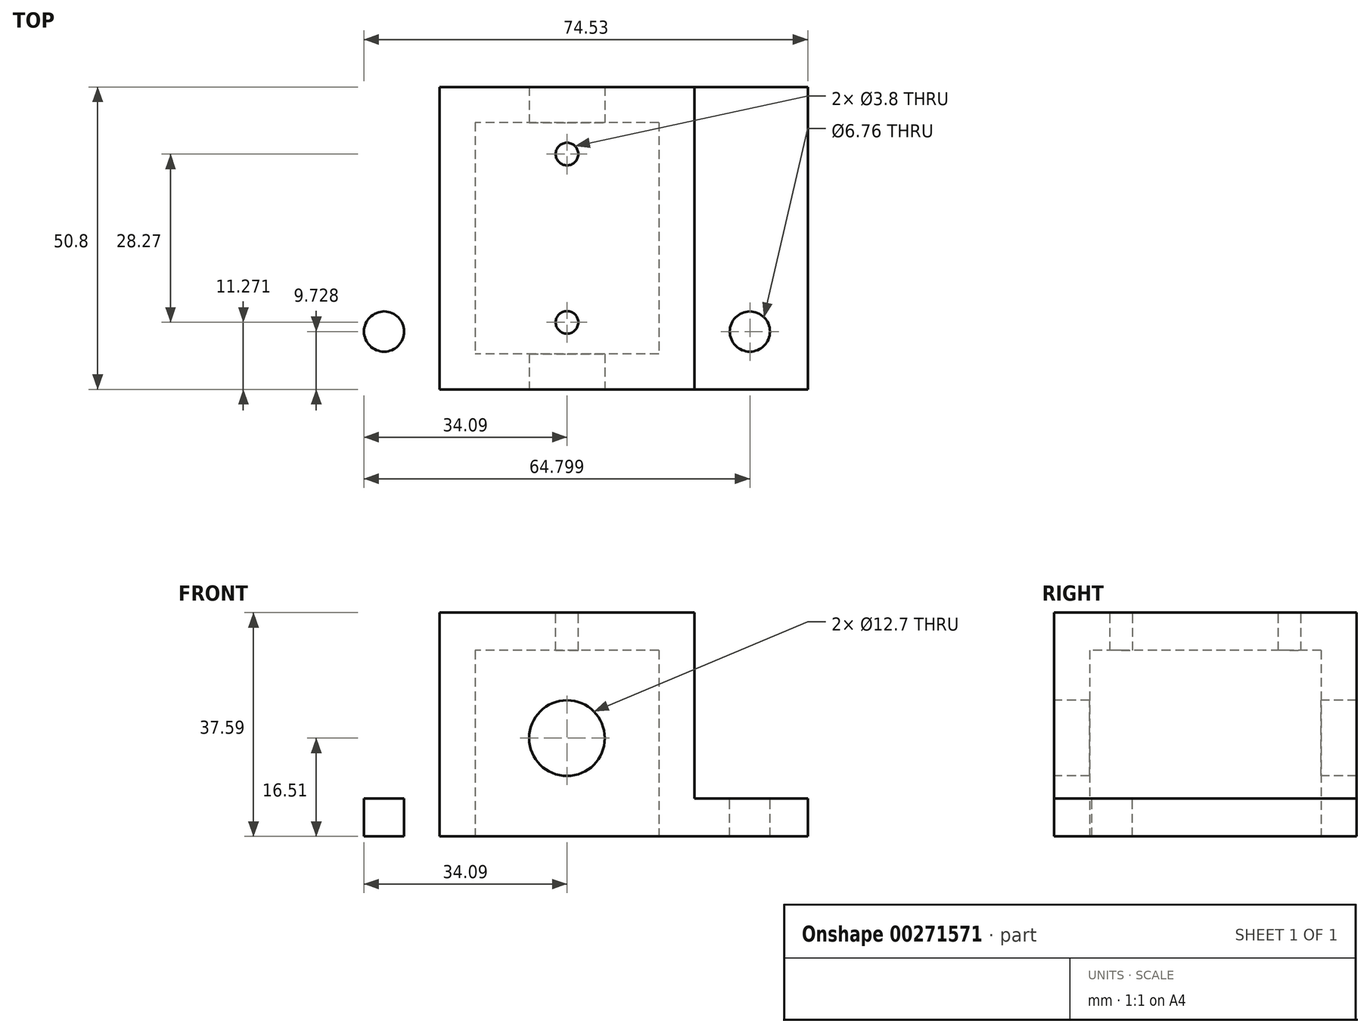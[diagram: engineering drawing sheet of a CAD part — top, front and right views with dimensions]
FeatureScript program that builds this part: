
annotation { "Feature Type Name" : "Feature", "Feature Type Description" : "" }
export const myFeature = defineFeature(function(context is Context, id is Id, definition is map)
    precondition{}
    {
        {
            var Q0;
            Q0=qCreatedBy(makeId("Top.planeOp"),FACE);
            var sketch = newSketch(context, id + "F0", { "sketchPlane" : qUnion([Q0])});
            skLineSegment(sketch, "E0.bottom", {"start": v(40.44, -25.4) * mm, "end": v(-40.44, -25.4) * mm});
            skLineSegment(sketch, "E0.top", {"start": v(40.44, 25.4) * mm, "end": v(-40.44, 25.4) * mm});
            skLineSegment(sketch, "E0.left", {"start": v(40.44, -25.4) * mm, "end": v(40.44, 25.4) * mm});
            skLineSegment(sketch, "E0.right", {"start": v(-40.44, -25.4) * mm, "end": v(-40.44, 25.4) * mm});
            skPoint(sketch, "E0.middle", {"position": v(0, 0) * mm});
            skSolve(sketch);
        }
        {
            var Q0;
            Q0=makeQuery(id+"F0.imprint","IMPRINT",FACE,{"disambiguationData":[TD([[makeQuery(id+"F0.imprint","IMPRINT",EDGE,{"derivedFrom":sQuery(id+"F0.wireOp",EDGE,"E0.bottom")}),-1.0]])]});
            extrude(context, id + "F1", {"entities" : qUnion([Q0]), "depth" : 37.6 * mm});
        }
        {
            var Q0;
            Q0=makeQuery(id+"F1.opExtrude","CAP_FACE",FACE,{"disambiguationData":[OSD([sQuery(id+"F0.wireOp",EDGE,"E0.bottom"),sQuery(id+"F0.wireOp",EDGE,"E0.top"),sQuery(id+"F0.wireOp",EDGE,"E0.left"),sQuery(id+"F0.wireOp",EDGE,"E0.right")])],"isStart":false});
            var sketch = newSketch(context, id + "F2", { "sketchPlane" : qUnion([Q0])});
            skLineSegment(sketch, "E1.left", {"start": v(-40.44, 19.05) * mm, "end": v(-40.44, -19.05) * mm});
            skLineSegment(sketch, "E1.right", {"start": v(-21.39, 19.05) * mm, "end": v(-21.39, -19.05) * mm});
            skLineSegment(sketch, "E2", {"start": v(-21.39, 19.05) * mm, "end": v(-21.39, 25.4) * mm});
            skLineSegment(sketch, "E3", {"start": v(-21.39, -19.05) * mm, "end": v(-21.39, -25.4) * mm});
            skLineSegment(sketch, "E4", {"start": v(0, 15.68) * mm, "end": v(0, -17.66) * mm, "construction": true});
            skLineSegment(sketch, "E5.MirrorCS", {"start": v(21.39, 19.05) * mm, "end": v(21.39, -19.05) * mm});
            skLineSegment(sketch, "E6.MirrorCS", {"start": v(40.44, 19.05) * mm, "end": v(40.44, -19.05) * mm});
            skLineSegment(sketch, "E7", {"start": v(21.39, 19.05) * mm, "end": v(21.39, 25.4) * mm});
            skLineSegment(sketch, "E8", {"start": v(21.39, -19.05) * mm, "end": v(21.39, -25.4) * mm});
            skSolve(sketch);
        }
        {
            var Q0;
            Q0=makeQuery(id+"F2.imprint","IMPRINT",FACE,{"disambiguationData":[TD([[makeQuery(id+"F2.imprint","IMPRINT",EDGE,{"derivedFrom":sQuery(id+"F2.wireOp",EDGE,"E1.bottom")}),-1.0]])]});
            var Q1;
            Q1=makeQuery(id+"F2.imprint","IMPRINT",FACE,{"disambiguationData":[TD([[makeQuery(id+"F2.imprint","IMPRINT",EDGE,{"derivedFrom":sQuery(id+"F2.wireOp",EDGE,"E5.MirrorCS")}),1.0]])]});
            extrude(context, id + "F3", {"entities" : qUnion([Q0, Q1]), "operationType" : NewBodyOperationType.REMOVE, "oppositeDirection" : true, "depth" : 31.24 * mm});
        }
        {
            var Q0;
            Q0=makeQuery(id+"F1.opExtrude","CAP_FACE",FACE,{"disambiguationData":[OSD([sQuery(id+"F0.wireOp",EDGE,"E0.bottom"),sQuery(id+"F0.wireOp",EDGE,"E0.top"),sQuery(id+"F0.wireOp",EDGE,"E0.left"),sQuery(id+"F0.wireOp",EDGE,"E0.right")])],"isStart":true});
            var sketch = newSketch(context, id + "F4", { "sketchPlane" : qUnion([Q0])});
            skLineSegment(sketch, "E9.bottom", {"start": v(15.43, -19.45) * mm, "end": v(-15.43, -19.45) * mm});
            skLineSegment(sketch, "E9.top", {"start": v(15.43, 19.45) * mm, "end": v(-15.43, 19.45) * mm});
            skLineSegment(sketch, "E9.left", {"start": v(15.43, -19.45) * mm, "end": v(15.43, 19.45) * mm});
            skLineSegment(sketch, "E9.right", {"start": v(-15.43, -19.45) * mm, "end": v(-15.43, 19.45) * mm});
            skPoint(sketch, "E9.middle", {"position": v(0, 0) * mm});
            skSolve(sketch);
        }
        {
            var Q0;
            Q0=makeQuery(id+"F4.imprint","IMPRINT",FACE,{"disambiguationData":[TD([[makeQuery(id+"F4.imprint","IMPRINT",EDGE,{"derivedFrom":sQuery(id+"F4.wireOp",EDGE,"E9.bottom")}),-1.0]])]});
            extrude(context, id + "F5", {"entities" : qUnion([Q0]), "operationType" : NewBodyOperationType.REMOVE, "oppositeDirection" : true, "depth" : 31.24 * mm});
        }
        {
            var Q0;
            Q0=makeQuery(id+"F1.opExtrude","SWEPT_FACE",FACE,{"disambiguationData":[OSD([sQuery(id+"F0.wireOp",EDGE,"E0.bottom")])]});
            var sketch = newSketch(context, id + "F6", { "sketchPlane" : qUnion([Q0])});
            skLineSegment(sketch, "E10", {"start": v(-21.38, 6.35) * mm, "end": v(-21.38, 0) * mm, "construction": true});
            skLineSegment(sketch, "E11", {"start": v(21.38, 6.35) * mm, "end": v(21.38, 0) * mm, "construction": true});
            skLineSegment(sketch, "E12", {"start": v(0, 0) * mm, "end": v(0, 10.16) * mm, "construction": true});
            skCircle(sketch, "E13", {"center": v(0, 16.51) * mm, "radius": 6.35 * mm});
            skPoint(sketch, "E13.second.point", {"position": v(0, 22.86) * mm});
            skPoint(sketch, "E13.third.point", {"position": v(6.01, 14.47) * mm});
            skLineSegment(sketch, "E14", {"start": v(0, 16.51) * mm, "end": v(0, 10.16) * mm, "construction": true});
            skSolve(sketch);
        }
        {
            var Q0;
            Q0=makeQuery(id+"F6.imprint","IMPRINT",FACE,{"disambiguationData":[TD([[makeQuery(id+"F6.imprint","IMPRINT",EDGE,{"derivedFrom":sQuery(id+"F6.wireOp",EDGE,"E13")}),1.0]])]});
            extrude(context, id + "F7", {"entities" : qUnion([Q0]), "operationType" : NewBodyOperationType.REMOVE, "oppositeDirection" : true, "depth" : 25400 * mm});
        }
        {
            var Q0;
            {var subQ5=sQuery(id+"F2.wireOp",EDGE,"E1.left");Q0=makeQuery(id+"F2.imprint","IMPRINT",FACE,{"disambiguationData":[TD([[makeQuery(id+"F2.imprint","IMPRINT",EDGE,{"derivedFrom":subQ5}),-1.0]])]});}
            extrude(context, id + "F8", {"entities" : qUnion([Q0]), "operationType" : NewBodyOperationType.REMOVE, "oppositeDirection" : true, "depth" : 31.24 * mm});
        }
        {
            var Q0;
            Q0=makeQuery(id+"F2.imprint","IMPRINT",FACE,{"disambiguationData":[TD([[makeQuery(id+"F2.imprint","IMPRINT",EDGE,{"derivedFrom":sQuery(id+"F2.wireOp",EDGE,"E1.right")}),1.0]])]});
            var sketch = newSketch(context, id + "F9", { "sketchPlane" : qUnion([Q0])});
            skCircle(sketch, "E15", {"center": v(0, 14.14) * mm, "radius": 1.9 * mm});
            skCircle(sketch, "E16", {"center": v(0, -14.13) * mm, "radius": 1.9 * mm});
            skLineSegment(sketch, "E17", {"start": v(0, 12.24) * mm, "end": v(0, -12.23) * mm, "construction": true});
            skSolve(sketch);
        }
        {
            var Q0;
            Q0=makeQuery(id+"F9.imprint","IMPRINT",FACE,{"disambiguationData":[TD([[makeQuery(id+"F9.imprint","IMPRINT",EDGE,{"derivedFrom":sQuery(id+"F9.wireOp",EDGE,"E15")}),1.0]])]});
            var Q1;
            Q1=makeQuery(id+"F9.imprint","IMPRINT",FACE,{"disambiguationData":[TD([[makeQuery(id+"F9.imprint","IMPRINT",EDGE,{"derivedFrom":sQuery(id+"F9.wireOp",EDGE,"E16")}),1.0]])]});
            extrude(context, id + "F10", {"entities" : qUnion([Q0, Q1]), "operationType" : NewBodyOperationType.REMOVE, "oppositeDirection" : true, "depth" : 25.4 * mm});
        }
        {
            var Q0;
            Q0=makeQuery(id+"F8.boolean.opBoolean","COPY",FACE,{"derivedFrom":makeQuery(id+"F8.opExtrude","CAP_FACE",FACE,{"disambiguationData":[OSD([sQuery(id+"F0.wireOp",EDGE,"E0.bottom"),sQuery(id+"F0.wireOp",EDGE,"E0.top"),sQuery(id+"F0.wireOp",EDGE,"E0.right"),sQuery(id+"F2.wireOp",EDGE,"E1.left"),sQuery(id+"F2.wireOp",EDGE,"E1.right"),sQuery(id+"F2.wireOp",EDGE,"E2"),sQuery(id+"F2.wireOp",EDGE,"E3")])],"isStart":false})});
            var sketch = newSketch(context, id + "F11", { "sketchPlane" : qUnion([Q0])});
            skCircle(sketch, "E18", {"center": v(-30.7, 15.67) * mm, "radius": 3.38 * mm});
            skLineSegment(sketch, "E19", {"start": v(-38.7, 25.4) * mm, "end": v(-26.7, 25.4) * mm, "construction": true});
            skLineSegment(sketch, "E20", {"start": v(-40.44, 20.08) * mm, "end": v(-40.44, 8.53) * mm, "construction": true});
            skLineSegment(sketch, "E21", {"start": v(-39.4, 0) * mm, "end": v(-25.33, 0) * mm, "construction": true});
            skPoint(sketch, "E21.endSnap0", {"position": v(-40.44, 0) * mm});
            skCircle(sketch, "E22.MirrorC", {"center": v(-30.7, -15.67) * mm, "radius": 3.38 * mm});
            skLineSegment(sketch, "E23", {"start": v(0, 8.95) * mm, "end": v(0, -8.66) * mm, "construction": true});
            skCircle(sketch, "E24.MirrorC", {"center": v(30.7, 15.67) * mm, "radius": 3.38 * mm});
            skCircle(sketch, "E25.MirrorC", {"center": v(30.7, -15.67) * mm, "radius": 3.38 * mm});
            skSolve(sketch);
        }
        {
            var Q0;
            Q0=makeQuery(id+"F11.imprint","IMPRINT",FACE,{"disambiguationData":[TD([[makeQuery(id+"F11.imprint","IMPRINT",EDGE,{"derivedFrom":sQuery(id+"F11.wireOp",EDGE,"E18")}),1.0]])]});
            var Q1;
            Q1=makeQuery(id+"F11.imprint","IMPRINT",FACE,{"disambiguationData":[TD([[makeQuery(id+"F11.imprint","IMPRINT",EDGE,{"derivedFrom":sQuery(id+"F11.wireOp",EDGE,"E22.MirrorC")}),-1.0]])]});
            var Q2;
            Q2=makeQuery(id+"F11.imprint","IMPRINT",FACE,{"disambiguationData":[TD([[makeQuery(id+"F11.imprint","IMPRINT",EDGE,{"derivedFrom":sQuery(id+"F11.wireOp",EDGE,"E24.MirrorC")}),-1.0]])]});
            var Q3;
            Q3=makeQuery(id+"F11.imprint","IMPRINT",FACE,{"disambiguationData":[TD([[makeQuery(id+"F11.imprint","IMPRINT",EDGE,{"derivedFrom":sQuery(id+"F11.wireOp",EDGE,"E25.MirrorC")}),1.0]])]});
            extrude(context, id + "F12", {"entities" : qUnion([Q0, Q1, Q2, Q3]), "operationType" : NewBodyOperationType.REMOVE, "oppositeDirection" : true, "depth" : 25.4 * mm});
        }
    });
